# Revit family: 1SE_Trez_TC_2C_T_500_With_Ramp
name_source: partatom
category: Specialty Equipment
units: mm (PartAtom-declared; Revit-internal decimal feet)

## family parameters
Always vertical = Yes
Cut with Voids When Loaded = Yes
Part Type = Normal
Room Calculation Point = No
Round Connector Dimension = Use Diameter
Shared = No
Work Plane-Based = No

## types (5) — shared parameters
Cabin = Speciality_Equipment_Trez_Cabin : Cabin
Cabin or Platform Back = Yes
Clearance = 365 mm  [stored 1.19751 ft]
Description = Trez Compact 2 Cylinders Tower. Goods only lift.
Manufacturer = TREZ Ltd.
Model = TC 2C T 500
Platform = Speciality_Equipment_Trez_Platform : Platform
Platform Material = TREZ_Steel
Profiles Material = TREZ_Steel
Ramp Height = 120 mm  [stored 0.393701 ft]
Ramp Material = TREZ_Steel
Safe Working Load = 500.00 kg
Tower Cladding Material = TREZ_Steel_Cladding
Travel = 4500 mm
URL = https://trez.bg

## per-type parameters (varying)
| type | Cabin or Platform | Clear Depth | Clear Width | Door Clear Height | Door Clear Width | Headroom | Rail Height | Ramp Width | Real Depth | Real Width | Safe Space | Tower Depth | Tower Width |
| Platform-3600x2900mm with Door Height 2500mm | Speciality_Equipment_Trez_Platform : Platform | 2900 mm  [stored 9.51444 ft] | 3600 mm  [stored 11.811 ft] | 2500 mm  [stored 8.2021 ft] | 3600 mm  [stored 11.811 ft] | 3100 mm  [stored 10.1706 ft] | 7600 mm  [stored 24.9344 ft] | 4080 mm  [stored 13.3858 ft] | 2900 mm  [stored 9.51444 ft] | 3600 mm  [stored 11.811 ft] | 600 mm | 3080 mm  [stored 10.105 ft] | 4330 mm  [stored 14.206 ft] |
| Cabin-1200x1800mm with Door Height 2000mm | Speciality_Equipment_Trez_Cabin : Cabin | 1800 mm  [stored 5.90551 ft] | 1200 mm  [stored 3.93701 ft] | 2000 mm  [stored 6.56168 ft] | 1200 mm  [stored 3.93701 ft] | 2900 mm  [stored 9.51444 ft] | 7400 mm  [stored 24.2782 ft] | 1680 mm  [stored 5.51181 ft] | 1800 mm  [stored 5.90551 ft] | 1200 mm  [stored 3.93701 ft] | 900 mm  [stored 2.95276 ft] | 1980 mm  [stored 6.49606 ft] | 1930 mm  [stored 6.33202 ft] |
| Cabin-2400x1800mm with Door Height 2000mm | Speciality_Equipment_Trez_Cabin : Cabin | 1800 mm  [stored 5.90551 ft] | 2400 mm | 2000 mm  [stored 6.56168 ft] | 2400 mm | 2900 mm  [stored 9.51444 ft] | 7400 mm  [stored 24.2782 ft] | 2880 mm  [stored 9.44882 ft] | 1800 mm  [stored 5.90551 ft] | 2400 mm | 900 mm  [stored 2.95276 ft] | 1980 mm  [stored 6.49606 ft] | 3130 mm  [stored 10.269 ft] |
| Platform-2400x1800mm with Door Height 2000mm | Speciality_Equipment_Trez_Platform : Platform | 1800 mm  [stored 5.90551 ft] | 2400 mm | 2000 mm  [stored 6.56168 ft] | 2400 mm | 2600 mm  [stored 8.53018 ft] | 7100 mm  [stored 23.294 ft] | 2880 mm  [stored 9.44882 ft] | 1800 mm  [stored 5.90551 ft] | 2400 mm | 600 mm | 1980 mm  [stored 6.49606 ft] | 3130 mm  [stored 10.269 ft] |
| Platform-1300x2400mm with Door Height 2400mm | Speciality_Equipment_Trez_Platform : Platform | 2400 mm | 1300 mm  [stored 4.26509 ft] | 2400 mm | 1300 mm  [stored 4.26509 ft] | 3000 mm  [stored 9.84252 ft] | 7500 mm  [stored 24.6063 ft] | 1780 mm  [stored 5.8399 ft] | 2400 mm | 1300 mm  [stored 4.26509 ft] | 600 mm | 2580 mm | 2030 mm  [stored 6.6601 ft] |

note: [stored X ft] marks values corroborated as IEEE doubles in the binary element streams (Revit-internal decimal feet)

## geometry (parser evidence)
native form markers: Sweep x11
no freeform markers — native parametric forms only
